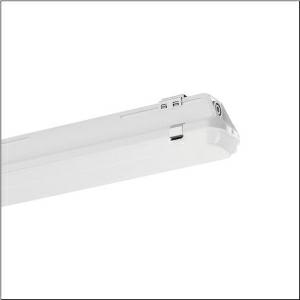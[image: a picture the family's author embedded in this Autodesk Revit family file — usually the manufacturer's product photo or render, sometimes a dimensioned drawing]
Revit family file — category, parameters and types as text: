
# Revit family: monsun_21_parking_51fg207l430k
name_source: partatom
category: Lighting Fixtures
units: mm (PartAtom-declared; Revit-internal decimal feet)

## family parameters
Cut with Voids When Loaded = No
Host = Face
Light Source = No
Part Type = Normal
Room Calculation Point = No
Round Connector Dimension = Use Diameter
Shared = No

## types (1)
- Monsun 21 parking (1 x LED, 3930 lm, 24.7 W, 4000K)
    Apparent Load = 25 VA
    CIE Flux Codes = 45 75 93 94 100
    Color Rendering = 80
    Color Temperature = 4000K
    Default Elevation = 1800 mm
    Description = Monsun 21 parking, damp-proof luminaire, chain hanger, primary optical cover: enclosure, of PC, light emission: direct distribution, primary light characteristic: symmetric, installation type: suspended mounting, surface-mounted, horizontal mounting, vertical mounting, LED, rated luminous flux: 3.930lm, luminous efficacy: 159lm/W, light colour: 840, colour temperature: 4000K, control gear: ON/OFF, with terminal, 3-pole, max. 2.5mm², mains connection: 220..240V, AC, 50/60Hz, rated input power: 25W, housing, of glass-fibre reinforced plastic, uncoated, bright grey, incl. chain hanger, length: 1.299mm, width: 90mm, height: 88mm, clip for enclosure, of stainless steel (V2A), ceiling mounting element, of stainless steel (V2A), chain hanger, of stainless steel (V2A), protection rating (complete): IP66, insulation class (complete): insulation class I (protective earthing), certification: CE, ENEC, VDE, UKCA, protection symbol: D, impact resistance: IK08, permissible operating ambient temperature: -25..+35°C, standard: EN 50419, EN 60598-2-1, corresponds to IFS (International Featured Standards) requirements for safety and quality in the food industry, for indoor or canopied outdoor use, no direct snow, no direct sun, no direct rain, LABS conformity tested according to VDMA 24364:2018-05, contact your sales advisor before using the luminaires in applications with unclear chemical exposure, large temperature fluctuations or condensation-forming humidity, packaging unit: 1 piece
    Height = 88 mm
    Lamp = 1 x LED
    Lamp Light Flux = 3930 lm
    Lamp Power = 24.7 W
    Lamp count = 1
    Length = 1299 mm
    Luminous efficacy = 159 lm/W
    Manufacturer = Siteco
    ModVariant = No
    Model = 51FG207L430K
    Mounting Place = Ceiling
    Mounting Type = Surface mounted
    Number of Poles = 1
    OnlyDefault = Yes
    Power Factor = 1
    Product Name = Monsun 21 parking
    Product group = damp-proof luminaire
    ProductGroupID = 300
    Protection Class = Protection class I
    Protection Degree = IP 66
    RLX_Detail_Level = 1
    RLX_Emergency_Light_Flux = 0 lm
    RLX_Emergency_Type = 0
    RLX_Emergency_Type_DB = No
    RlxData = <blob elided: 89657 chars, md5=8597dcdf>
    Socket = socket
    Standby Power = 0 W
    System Light Flux = 3930 lm
    System Power = 25 W
    Type Comments = Product without accessories
    Type Image = l_1319656.jpg
    URL = http://relux.com
    VarID = ---
    Voltage = 0 V
    Weight = 0.00 kg
    Width = 90 mm

## geometry (parser evidence)
native form markers: Blend x4, Sweep x11
no freeform markers — native parametric forms only
